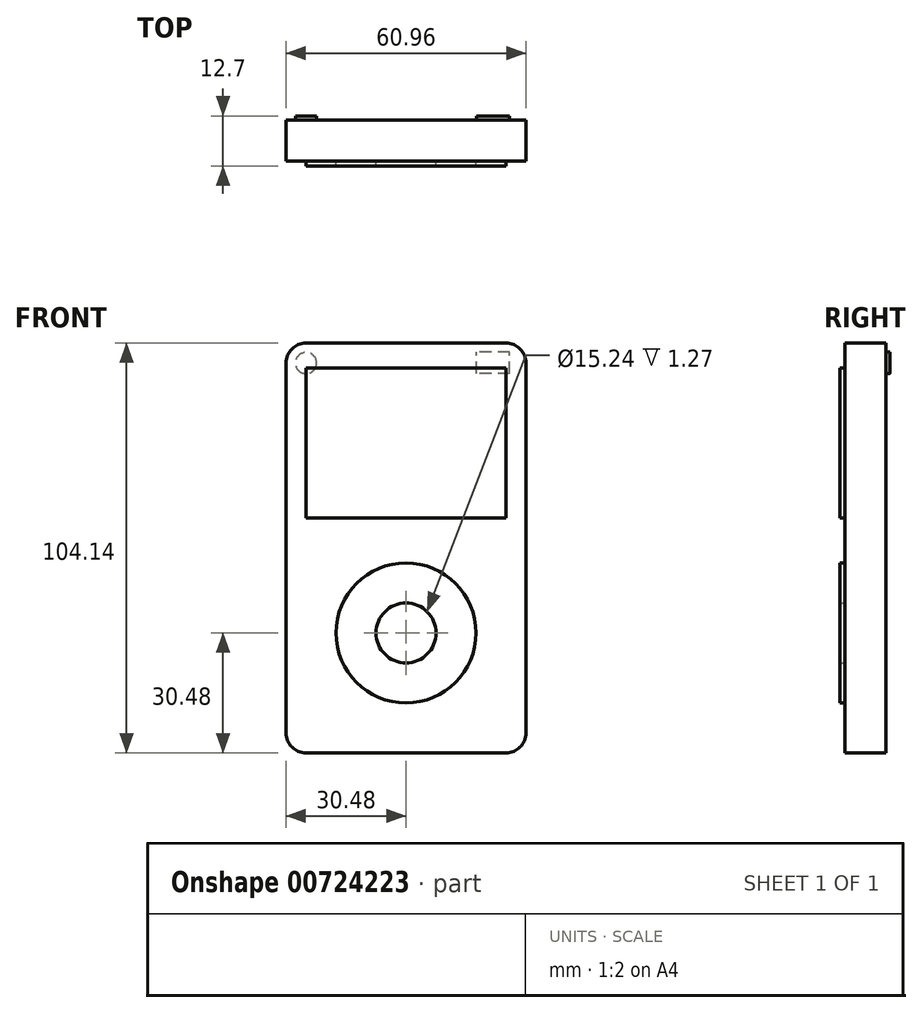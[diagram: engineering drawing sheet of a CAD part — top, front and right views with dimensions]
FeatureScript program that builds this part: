
annotation { "Feature Type Name" : "Feature", "Feature Type Description" : "" }
export const myFeature = defineFeature(function(context is Context, id is Id, definition is map)
    precondition{}
    {
        {
            var Q0;
            Q0=qCreatedBy(makeId("Front.planeOp"),FACE);
            var sketch = newSketch(context, id + "F0", { "sketchPlane" : qUnion([Q0])});
            skLineSegment(sketch, "E0.bottom", {"start": v(25.4, 52.07) * mm, "end": v(-25.4, 52.07) * mm});
            skLineSegment(sketch, "E0.top", {"start": v(25.4, -52.07) * mm, "end": v(-25.4, -52.07) * mm});
            skLineSegment(sketch, "E0.left", {"start": v(30.48, 47) * mm, "end": v(30.48, -47) * mm});
            skLineSegment(sketch, "E0.right", {"start": v(-30.48, 46.99) * mm, "end": v(-30.48, -47) * mm});
            skPoint(sketch, "E0.middle", {"position": v(0, 0) * mm});
            skPoint(sketch, "E1.visualSharp", {"position": v(-30.48, 52.07) * mm});
            skArc(sketch, "E1.filletArc", {"start": v(-25.4, 52.07) * mm, "mid": v(-29, 50.58) * mm, "end": v(-30.48, 46.99) * mm});
            skPoint(sketch, "E2.visualSharp", {"position": v(30.48, 52.07) * mm});
            skArc(sketch, "E2.filletArc", {"start": v(30.48, 47) * mm, "mid": v(29, 50.58) * mm, "end": v(25.4, 52.07) * mm});
            skPoint(sketch, "E3.visualSharp", {"position": v(30.48, -52.07) * mm});
            skArc(sketch, "E3.filletArc", {"start": v(25.4, -52.07) * mm, "mid": v(29, -50.58) * mm, "end": v(30.48, -47) * mm});
            skPoint(sketch, "E4.visualSharp", {"position": v(-30.48, -52.07) * mm});
            skArc(sketch, "E4.filletArc", {"start": v(-30.48, -47) * mm, "mid": v(-29, -50.58) * mm, "end": v(-25.4, -52.07) * mm});
            skSolve(sketch);
        }
        {
            var Q0;
            Q0 = qSketchRegion(id + "F0", true);
            extrude(context, id + "F1", {"entities" : qUnion([Q0]), "depth" : 10.4 * mm, "offsetDistance" : 25.4 * mm});
        }
        {
            var Q0;
            Q0=makeQuery(id+"F1.opExtrude","CAP_FACE",FACE,{"disambiguationData":[OSD([sQuery(id+"F0.wireOp",EDGE,"E0.bottom"),sQuery(id+"F0.wireOp",EDGE,"E0.top"),sQuery(id+"F0.wireOp",EDGE,"E0.left"),sQuery(id+"F0.wireOp",EDGE,"E0.right"),sQuery(id+"F0.wireOp",EDGE,"E1.filletArc"),sQuery(id+"F0.wireOp",EDGE,"E2.filletArc"),sQuery(id+"F0.wireOp",EDGE,"E3.filletArc"),sQuery(id+"F0.wireOp",EDGE,"E4.filletArc")])],"isStart":false});
            var sketch = newSketch(context, id + "F2", { "sketchPlane" : qUnion([Q0])});
            skLineSegment(sketch, "E5", {"start": v(-25.4, 45.72) * mm, "end": v(-25.4, 7.62) * mm});
            skLineSegment(sketch, "E6", {"start": v(-25.4, 7.62) * mm, "end": v(25.4, 7.62) * mm});
            skLineSegment(sketch, "E7", {"start": v(25.4, 7.62) * mm, "end": v(25.4, 45.72) * mm});
            skLineSegment(sketch, "E8", {"start": v(25.4, 45.72) * mm, "end": v(-25.4, 45.72) * mm});
            skPoint(sketch, "E9", {"position": v(0, 7.62) * mm});
            skPoint(sketch, "E10", {"position": v(-25.4, 26.67) * mm});
            skCircle(sketch, "E11", {"center": v(0, -21.6) * mm, "radius": 7.62 * mm});
            skCircle(sketch, "E12", {"center": v(0, -21.6) * mm, "radius": 17.78 * mm});
            skSolve(sketch);
        }
        {
            var Q0;
            Q0=makeQuery(id+"F2.imprint","IMPRINT",FACE,{"disambiguationData":[TD([[makeQuery(id+"F2.imprint","IMPRINT",EDGE,{"derivedFrom":sQuery(id+"F2.wireOp",EDGE,"E5")}),1.0]])]});
            var Q1;
            Q1=makeQuery(id+"F2.imprint","IMPRINT",FACE,{"disambiguationData":[TD([[makeQuery(id+"F2.imprint","IMPRINT",EDGE,{"derivedFrom":sQuery(id+"F2.wireOp",EDGE,"E11")}),-1.0]])]});
            extrude(context, id + "F3", {"entities" : qUnion([Q0, Q1]), "operationType" : NewBodyOperationType.ADD, "depth" : 1.27 * mm, "offsetDistance" : 25.4 * mm});
        }
        {
            var Q0;
            Q0=makeQuery(id+"F1.opExtrude","CAP_FACE",FACE,{"disambiguationData":[OSD([sQuery(id+"F0.wireOp",EDGE,"E0.bottom"),sQuery(id+"F0.wireOp",EDGE,"E0.top"),sQuery(id+"F0.wireOp",EDGE,"E0.left"),sQuery(id+"F0.wireOp",EDGE,"E0.right"),sQuery(id+"F0.wireOp",EDGE,"E1.filletArc"),sQuery(id+"F0.wireOp",EDGE,"E2.filletArc"),sQuery(id+"F0.wireOp",EDGE,"E3.filletArc"),sQuery(id+"F0.wireOp",EDGE,"E4.filletArc")])],"isStart":true});
            var sketch = newSketch(context, id + "F4", { "sketchPlane" : qUnion([Q0])});
            skCircle(sketch, "E13", {"center": v(25.4, 46.99) * mm, "radius": 2.7 * mm});
            skLineSegment(sketch, "E14.bottom", {"start": v(-26.32, 44.37) * mm, "end": v(-17.9, 44.37) * mm});
            skLineSegment(sketch, "E14.top", {"start": v(-26.32, 49.78) * mm, "end": v(-17.9, 49.78) * mm});
            skLineSegment(sketch, "E14.left", {"start": v(-26.32, 44.37) * mm, "end": v(-26.32, 49.78) * mm});
            skLineSegment(sketch, "E14.right", {"start": v(-17.9, 44.37) * mm, "end": v(-17.9, 49.78) * mm});
            skPoint(sketch, "E14.middle", {"position": v(-22.1, 47.07) * mm});
            skSolve(sketch);
        }
        {
            var Q0;
            Q0=makeQuery(id+"F4.imprint","IMPRINT",FACE,{"disambiguationData":[TD([[makeQuery(id+"F4.imprint","IMPRINT",EDGE,{"derivedFrom":sQuery(id+"F4.wireOp",EDGE,"E13")}),1.0]])]});
            var Q1;
            Q1=makeQuery(id+"F4.imprint","IMPRINT",FACE,{"disambiguationData":[TD([[makeQuery(id+"F4.imprint","IMPRINT",EDGE,{"derivedFrom":sQuery(id+"F4.wireOp",EDGE,"E14.bottom")}),1.0]])]});
            extrude(context, id + "F5", {"entities" : qUnion([Q0, Q1]), "operationType" : NewBodyOperationType.ADD, "depth" : 1.02 * mm, "offsetDistance" : 25.4 * mm});
        }
    });
